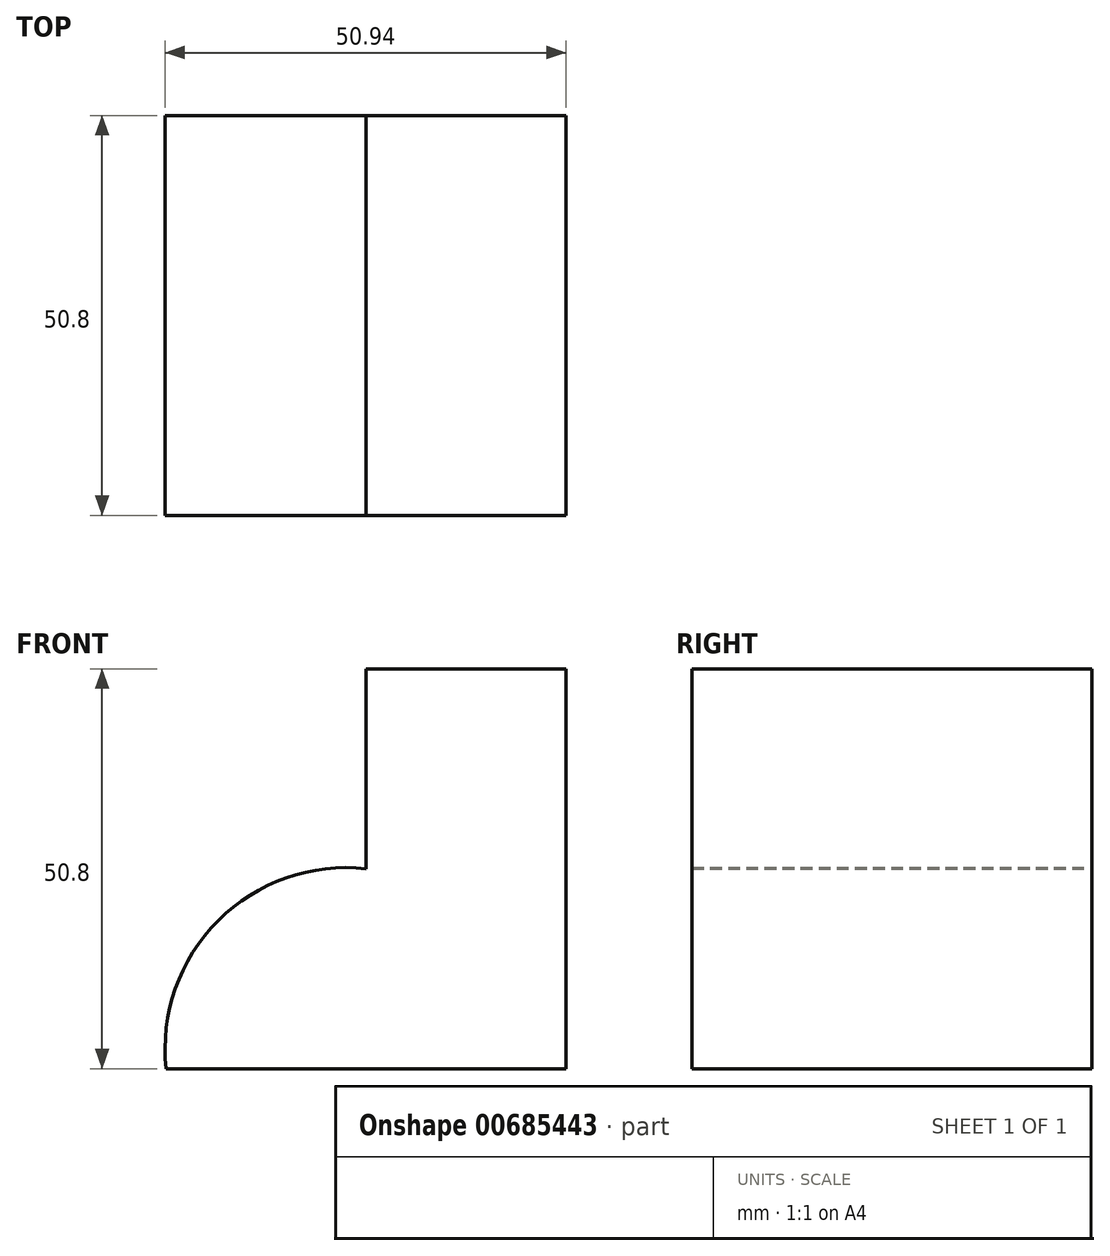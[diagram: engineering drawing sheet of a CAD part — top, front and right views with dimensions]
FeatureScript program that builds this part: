
annotation { "Feature Type Name" : "Feature", "Feature Type Description" : "" }
export const myFeature = defineFeature(function(context is Context, id is Id, definition is map)
    precondition{}
    {
        {
            var Q0;
            Q0=qCreatedBy(makeId("Front.planeOp"),FACE);
            var sketch = newSketch(context, id + "F0", { "sketchPlane" : qUnion([Q0])});
            skLineSegment(sketch, "E0", {"start": v(0, 75.98) * mm, "end": v(0, 25.18) * mm});
            skLineSegment(sketch, "E1", {"start": v(0, 75.98) * mm, "end": v(-25.4, 75.98) * mm});
            skLineSegment(sketch, "E2", {"start": v(0, 25.18) * mm, "end": v(-50.8, 25.18) * mm});
            skLineSegment(sketch, "E3", {"start": v(-25.4, 75.98) * mm, "end": v(-25.4, 50.58) * mm});
            skArc(sketch, "E4", {"start": v(-25.4, 50.58) * mm, "mid": v(-44.2, 43.98) * mm, "end": v(-50.8, 25.18) * mm});
            skSolve(sketch);
        }
        {
            var Q0;
            Q0=makeQuery(id+"F0.imprint","IMPRINT",FACE,{"disambiguationData":[TD([[makeQuery(id+"F0.imprint","IMPRINT",EDGE,{"derivedFrom":sQuery(id+"F0.wireOp",EDGE,"E0")}),-1.0]])]});
            extrude(context, id + "F1", {"entities" : qUnion([Q0]), "depth" : 50.8 * mm, "offsetDistance" : 25.4 * mm});
        }
    });
